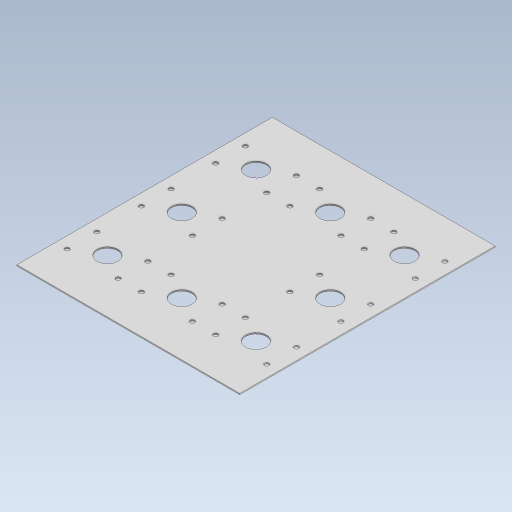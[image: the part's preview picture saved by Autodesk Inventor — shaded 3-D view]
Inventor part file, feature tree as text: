
AUTODESK INVENTOR PART (.ipt)
format: ipt  version: 2023 (Build 270158000, 158)  size: 184,832 bytes
history: native  units: in
note: dims shown in document units (in); Inventor stores cm internally (conversion verified against a paired STEP export)
features: extrude x2, sketch x2, projected_geometry x1
ambient origin geometry x8: Origin, YZ Plane, XZ Plane, XY Plane, X Axis, Y Axis, Z Axis, Center Point
bodies: Solid1 (feature_tree)
feature tree (5):
  extrude  "Extrusion1"  Depth=13.75in
  extrude  "Extrusion2"  Depth=0.0625in
  sketch  "Sketch1"  dims[d0=12.0in d1=13.75in]
  sketch  "Sketch2"  dims[d2=0.0625in d3=0.0in d4=1.125in d5=0.25in d6=0.8in d7=1.375in d8=2.0in d9=3.937in d10=1.9685in d11=10.5in d12=1.25in d13=1.1811in d15=4.0in d16=1.1811in d18=4.0in d21=0.0in d22=0.0in]
  projected_geometry  "Projected Loop1"
